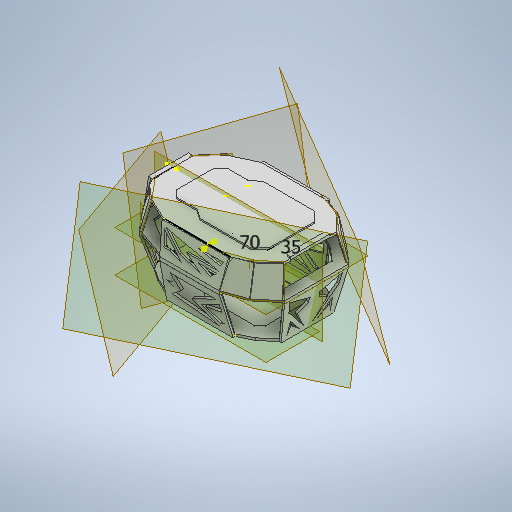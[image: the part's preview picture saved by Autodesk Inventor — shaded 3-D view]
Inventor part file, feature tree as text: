
AUTODESK INVENTOR PART (.ipt)
format: ipt  version: 2025.2 (Build 292293000, 293)  size: 6,166,528 bytes
history: native  units: mm
features: sketch x51, extrude x38, other x23, plane x17, loft x11, mirror x2, chamfer x2, fillet x2
ambient origin geometry x8: Origin, YZ Plane, XZ Plane, XY Plane, X Axis, Y Axis, Z Axis, Center Point
bodies: Body1 (feature_tree)
feature tree (146):
  extrude  "Extrusion2"  Depth=45.0mm
  extrude  "Extrusion3"  Depth=40.0mm
  plane  "Work Plane3"
  extrude  "Extrusion4"  Depth=145.0mm
  extrude  "Extrusion5"  Depth=55.0mm
  plane  "Work Plane4"
  extrude  "Extrusion6"  Depth=40.0mm
  sketch  "Sketch8"  dims[d17=165.0deg d18=15.0mm]
  sketch  "Sketch9"  dims[d20=10.0mm d21=40.0mm]
  sketch  "Sketch10"  dims[d22=5.0mm d23=5.0mm]
  loft  "Loft1"
  loft  "Loft2"
  extrude  "Extrusion7"  Depth=5.0mm
  extrude  "Extrusion8"  TaperAngle=90.0deg  [1 undecoded]
  extrude  "Extrusion9"  Depth=110.0mm
  sketch  "Sketch14"  dims[d30=45.0mm d31=20.0mm]
  sketch  "Sketch15"  dims[d32=45.0deg d39=5.0mm d40=0.0mm]
  sketch  "Sketch16"  dims[d41=3.0mm d42=3.0mm d43=0.0mm d44=0.0mm d45=150.0mm]
  loft  "Loft3"
  loft  "Loft4"
  loft  "Loft5"
  extrude  "Extrusion10"  Depth=150.0mm
  extrude  "Extrusion11"  Depth=10.0mm
  extrude  "Extrusion12"  Depth=10.0mm
  extrude  "Extrusion13"  Depth=10.0mm
  extrude  "Extrusion14"  Depth=10.0mm
  loft  "Loft7"
  loft  "Loft8"
  sketch  "Sketch22"  dims[d57=10.0mm d58=10.0mm]
  plane  "Work Plane5"
  extrude  "Extrusion15"  Depth=3.0mm TaperAngle=0.0deg
  plane  "Work Plane6"
  extrude  "Extrusion16"  Depth=10.0mm
  extrude  "Extrusion17"  Depth=70.0mm
  plane  "Work Plane7"
  extrude  "Extrusion18"  Depth=50.0mm
  sketch  "Sketch28"  dims[d71=27.925268mm d72=10.0mm]
  extrude  "Extrusion19"  Depth=10.0mm
  extrude  "Extrusion20"  Depth=60.0mm
  extrude  "Extrusion21"  Depth=5.0mm TaperAngle=0.0deg
  extrude  "Extrusion22"  TaperAngle=0.0deg  [1 undecoded]
  extrude  "Extrusion23"  TaperAngle=0.0deg  [1 undecoded]
  extrude  "Extrusion24"  Depth=4.0mm TaperAngle=0.0deg
  extrude  "Extrusion25"  TaperAngle=0.0deg  [1 undecoded]
  extrude  "Extrusion26"  TaperAngle=0.0deg  [1 undecoded]
  extrude  "Extrusion27"  TaperAngle=0.0deg  [1 undecoded]
  plane  "Work Plane8"
  mirror  "Mirror1"
  loft  "Loft9"
  loft  "Loft10"
  loft  "Loft11"
  loft  "Loft12"
  plane  "Work Plane14"
  plane  "Work Plane15"
  extrude  "Extrusion28"  TaperAngle=0.0deg  [1 undecoded]
  extrude  "Extrusion29"  Depth=4.0mm TaperAngle=0.0deg
  plane  "Work Plane16"
  extrude  "Extrusion30"  Depth=92.689mm
  mirror  "Mirror2"
  extrude  "Extrusion31"  Depth=70.0mm
  sketch  "Sketch42"  dims[d126=4.0mm d127=0.0mm d128=4.0mm d129=0.0mm]
  extrude  "Extrusion32"  Depth=10.0mm
  extrude  "Extrusion33"  Depth=70.0mm
  extrude  "Extrusion34"  Depth=35.0mm
  extrude  "Extrusion35"  Depth=23.0mm TaperAngle=0.0deg
  chamfer  "Chamfer1"  Distance=17.5mm
  extrude  "Extrusion36"  Depth=30.0mm
  chamfer  "Chamfer2"  Distance=20.0mm
  sketch  "Sketch48"  dims[d142=90.0deg d143=23.0mm d144=0.0mm]
  extrude  "Extrusion37"  TaperAngle=90.0deg  [1 undecoded]
  extrude  "Extrusion38"  Depth=3.0mm
  sketch  "Sketch51"  dims[d149=25.0mm d150=30.0mm]
  sketch  "Sketch52"  dims[d151=15.0deg]
  sketch  "Sketch53"  dims[d152=90.0deg]
  extrude  "Extrusion39"  Depth=3.0mm TaperAngle=0.0deg
  fillet  "Fillet1"  Radius=25.0mm
  fillet  "Fillet2"  [1 undecoded]
  sketch  "Sketch1"  dims[d6=115.0mm d8=45.0mm]
  other  "Image1"
  sketch  "Sketch3"  dims[d9=45.0deg d10=40.0mm]
  sketch  "Sketch4"  dims[d11=27.925268mm d12=145.0mm]
  sketch  "Sketch5"  dims[d13=27.052603mm d14=55.0mm]
  sketch  "Sketch6"  dims[d15=27.052603mm d16=40.0mm]
  other  "Edges1"
  other  "Edges2"
  other  "Edges3"
  other  "Edges4"
  sketch  "Sketch11"  dims[d24=40.0mm d25=90.0deg]
  sketch  "Sketch12"  dims[d26=30.0mm d27=110.0mm]
  sketch  "Sketch13"  dims[d28=25.0mm d29=25.307274mm]
  other  "Edges5"
  other  "Edges6"
  other  "Edges7"
  other  "Edges8"
  other  "Edges9"
  other  "Edges10"
  sketch  "Sketch17"  dims[d46=10.0mm d48=10.0mm]
  sketch  "Sketch18"  dims[d49=10.0mm d50=22.68928mm]
  sketch  "Sketch19"  dims[d51=10.0mm d52=10.0mm]
  sketch  "Sketch20"  dims[d53=10.0mm d54=10.0mm]
  sketch  "Sketch21"  dims[d55=10.0mm d56=10.0mm]
  other  "Edges13"
  other  "Edges14"
  other  "Edges15"
  other  "Edges16"
  sketch  "Sketch23"  dims[d59=5.0mm d60=0.0mm d61=3.0mm d62=3.0mm d63=0.0mm d64=0.0mm]
  sketch  "Sketch24"  dims[d65=-90.0mm d66=10.0mm]
  sketch  "Sketch25"  dims[d67=70.0mm d68=50.0mm]
  sketch  "Sketch26"  dims[d69=22.68928mm d70=50.0mm]
  sketch  "Sketch29"  dims[d73=50.0mm d74=60.0mm]
  sketch  "Sketch30"  dims[d75=70.0mm d76=5.0mm d77=0.0mm]
  sketch  "Sketch31"  dims[d78=0.0mm d79=90.0deg d80=0.0mm d81=90.0deg]
  sketch  "Sketch32"  dims[d82=0.0mm d83=90.0deg d84=0.0mm d85=90.0deg]
  sketch  "Sketch33"  dims[d86=4.0mm d87=0.0mm d88=4.0mm d89=0.0mm]
  sketch  "Sketch34"  dims[d90=4.0mm d91=0.0mm d92=0.0mm d93=90.0deg]
  sketch  "Sketch35"  dims[d94=0.0mm d95=90.0deg d96=0.0mm d97=90.0deg]
  sketch  "Sketch36"  dims[d98=0.0mm d99=90.0deg d100=0.0mm d101=90.0deg]
  sketch  "Sketch37"  dims[d102=0.0mm d103=90.0deg d104=4.0mm d105=0.0mm]
  plane  "Work Plane9"
  plane  "Work Plane10"
  plane  "Work Plane11"
  plane  "Work Plane12"
  plane  "Work Plane13"
  other  "Edges17"
  other  "Edges18"
  other  "Edges19"
  other  "Edges20"
  other  "Edges21"
  other  "Edges22"
  other  "Edges23"
  other  "Edges24"
  sketch  "Sketch38"  dims[d106=4.0mm d107=0.0mm d108=4.0mm d109=0.0mm]
  sketch  "Sketch39"  dims[d110=4.0mm d111=0.0mm d112=4.0mm d113=0.0mm]
  sketch  "Sketch40"  dims[d118=0.0mm d119=90.0deg d120=0.0mm d121=90.0deg]
  plane  "Work Plane17"
  plane  "Work Plane18"
  plane  "Work Plane19"
  sketch  "Sketch41"  dims[d122=0.0mm d123=90.0deg d124=0.0mm d125=90.0deg]
  sketch  "Sketch43"  dims[d130=4.0mm d131=0.0mm d132=92.689mm]
  sketch  "Sketch44"  dims[d133=4.0mm d134=0.0mm d135=70.0mm]
  sketch  "Sketch45"  dims[d136=35.0mm d137=10.0mm]
  sketch  "Sketch46"  dims[d138=50.0mm d139=70.0mm]
  sketch  "Sketch47"  dims[d140=50.0mm d141=35.0mm]
  sketch  "Sketch49"  dims[d145=70.0mm]
  sketch  "Sketch50"  dims[d146=3.0mm d147=17.5mm d148=0.0mm]
  sketch  "Sketch54"  dims[d153=5.0mm d154=20.0mm d155=90.0deg d156=4.363323mm d157=17.5mm d158=0.0mm d159=25.0mm d160=165.0deg d161=40.0mm d162=150.0deg d163=50.0mm d164=1.745329mm d165=40.0mm d166=5.0mm d167=40.0mm d168=30.543262mm d169=17.5mm d170=0.0mm d171=10.0mm d172=100.0mm d173=150.0deg d174=40.0mm d175=19.198622mm d176=100.0mm d177=70.0mm d178=30.0deg d179=100.0mm d180=10.0mm d181=10.0mm d182=10.0mm d183=4.363323mm d184=40.0mm d185=40.0mm d186=6.981317mm d187=20.0mm d188=24.43461mm d189=16.0mm d190=10.0mm d191=0.0mm d192=80.0mm d193=24.43461mm d194=120.0mm d195=30.0deg d196=40.0mm d197=30.0deg d198=50.0mm d199=10.0mm d200=50.0mm d201=55.0mm d202=1.745329mm d203=30.0mm d204=27.925268mm d205=40.0mm d206=5.0mm d207=30.0mm d208=30.0mm d209=17.453293mm d210=60.0mm d211=30.0mm d212=50.0mm d213=0.0mm d214=10.0mm d215=10.0mm d216=10.0mm d217=10.0mm d218=90.0deg d219=10.0mm d220=20.0mm d221=10.0mm d222=17.453293mm d223=25.0mm d224=22.68928mm d225=70.0mm d226=10.0mm d227=40.0mm d228=22.68928mm d229=20.0mm d230=75.0deg d231=50.0mm d232=0.0mm d233=5.0mm d234=0.0mm d235=5.0mm d236=0.0mm d238=0.0mm d239=90.0deg d240=0.0mm d241=90.0deg d242=0.0mm d243=90.0deg d244=0.0mm d245=90.0deg d246=0.0mm d247=90.0deg d248=0.0mm d249=90.0deg d250=0.0mm d251=90.0deg d252=0.0mm d253=90.0deg d254=3.0mm d255=0.0mm d256=3.0mm d257=0.0mm d258=3.0mm d259=0.0mm d260=30.0mm d261=50.0mm d262=90.0mm d263=30.0mm d264=5.0mm d265=0.0mm d266=20.0mm d267=100.0mm d268=20.0mm d269=100.0mm d270=30.0mm d271=40.0mm d272=30.0mm d273=5.0mm d274=5.0mm d275=0.0mm d276=0.0mm d277=10.0mm d278=10.0mm d279=30.0mm d280=0.0mm d281=20.0mm d282=20.0mm d283=20.0mm d284=90.0deg d285=10.0mm d286=0.0mm d287=20.0mm d288=100.0mm d289=0.0mm d290=10.0mm d291=10.0mm d292=10.0mm d293=0.0mm d294=6.0mm d295=2.0mm d296=45.0deg d297=20.0mm d298=13.0mm d299=20.0mm d300=13.0mm d301=20.0mm d302=13.0mm d303=20.0mm d304=13.0mm d305=20.0mm d306=0.0mm d307=20.0mm d308=2.0mm d309=45.0deg d310=140.0mm d311=10.0mm d312=23.0mm d313=0.0mm d314=50.0mm d315=0.0mm d316=3.0mm d317=0.0mm d318=3.0mm d319=3.0mm]
note: 9 required parameter values undecoded (feature->parameter linkage not recoverable at this tier; creation-order binding heuristic only, values carry confidence <= 0.55)
